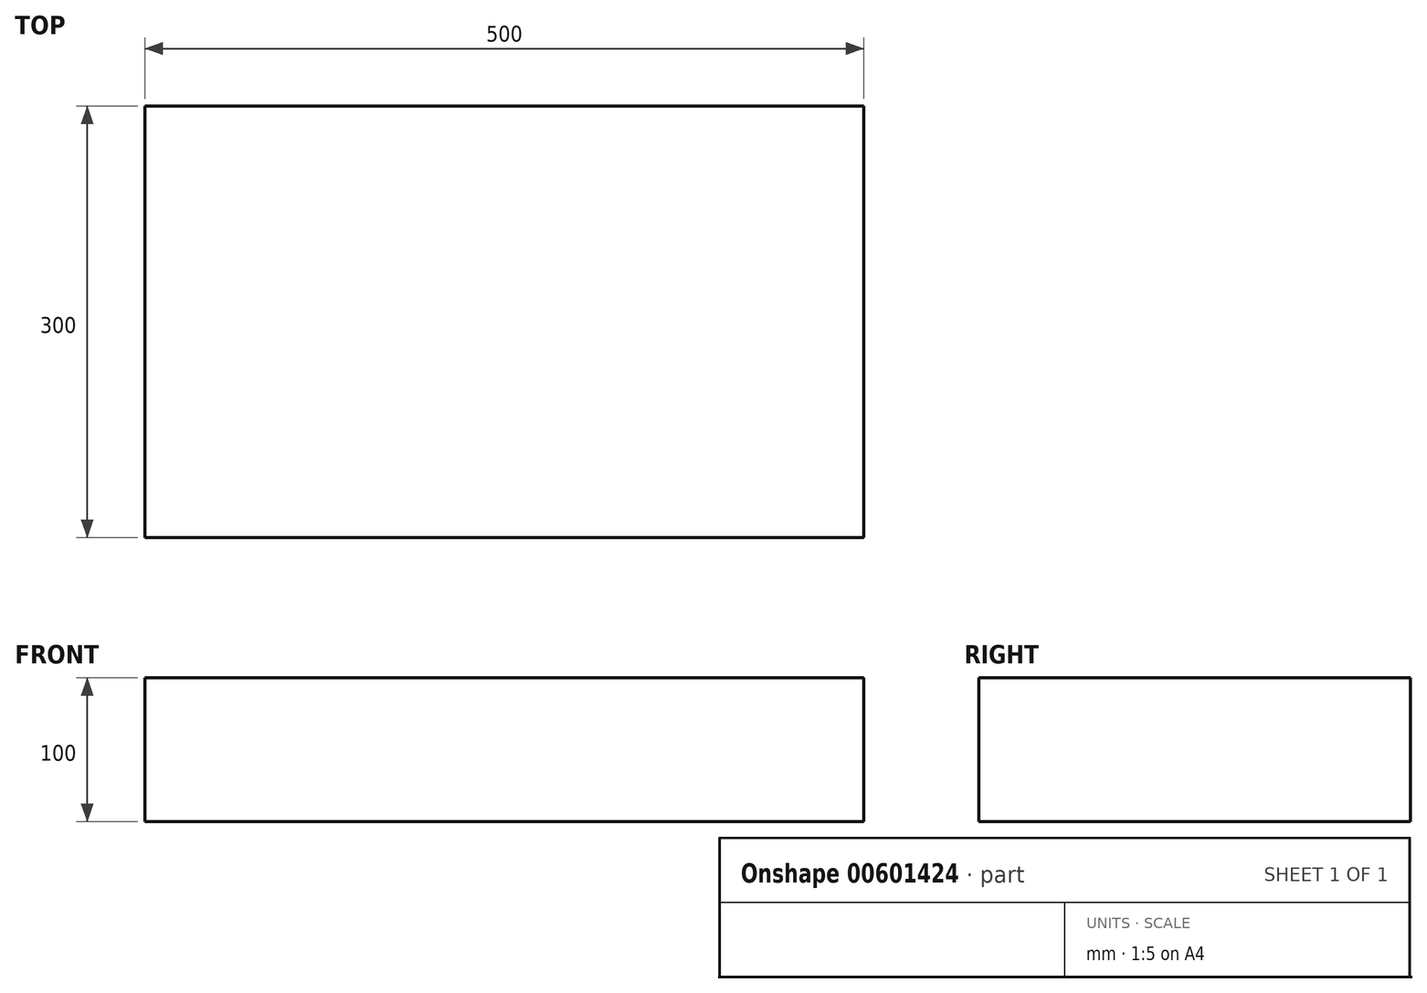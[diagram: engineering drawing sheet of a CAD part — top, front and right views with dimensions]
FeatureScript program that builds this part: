
annotation { "Feature Type Name" : "Feature", "Feature Type Description" : "" }
export const myFeature = defineFeature(function(context is Context, id is Id, definition is map)
    precondition{}
    {
        {
            var Q0;
            Q0=qCreatedBy(makeId("Top.planeOp"),FACE);
            var sketch = newSketch(context, id + "F0", { "sketchPlane" : qUnion([Q0])});
            skLineSegment(sketch, "E0.bottom", {"start": v(0, 0) * mm, "end": v(500, 0) * mm});
            skLineSegment(sketch, "E0.top", {"start": v(0, 300) * mm, "end": v(500, 300) * mm});
            skLineSegment(sketch, "E0.left", {"start": v(0, 0) * mm, "end": v(0, 300) * mm});
            skLineSegment(sketch, "E0.right", {"start": v(500, 0) * mm, "end": v(500, 300) * mm});
            skSolve(sketch);
        }
        {
            var Q0;
            Q0=makeQuery(id+"F0.imprint","IMPRINT",FACE,{"disambiguationData":[TD([[makeQuery(id+"F0.imprint","IMPRINT",EDGE,{"derivedFrom":sQuery(id+"F0.wireOp",EDGE,"E0.bottom")}),1.0]])]});
            extrude(context, id + "F1", {"entities" : qUnion([Q0]), "depth" : 100 * mm, "offsetDistance" : 25 * mm});
        }
    });
